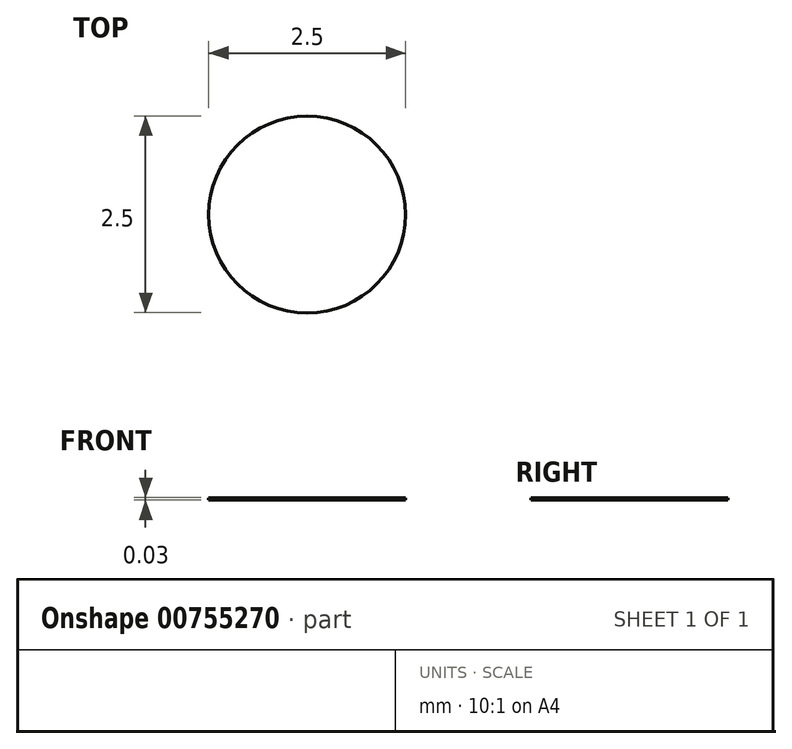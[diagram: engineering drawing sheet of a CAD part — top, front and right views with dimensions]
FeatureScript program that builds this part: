
annotation { "Feature Type Name" : "Feature", "Feature Type Description" : "" }
export const myFeature = defineFeature(function(context is Context, id is Id, definition is map)
    precondition{}
    {
        {
            var Q0;
            Q0=qCreatedBy(makeId("Top.planeOp"),FACE);
            var sketch = newSketch(context, id + "F0", { "sketchPlane" : qUnion([Q0])});
            skCircle(sketch, "E0", {"center": v(-41.46, 15.7) * mm, "radius": 1.25 * mm});
            skSolve(sketch);
        }
        {
            var Q0;
            Q0=makeQuery(id+"F0.imprint","IMPRINT",FACE,{"disambiguationData":[TD([[makeQuery(id+"F0.imprint","IMPRINT",EDGE,{"derivedFrom":sQuery(id+"F0.wireOp",EDGE,"E0")}),1.0]])]});
            extrude(context, id + "F1", {"entities" : qUnion([Q0]), "depth" : 3 / 101.6 * mm, "offsetDistance" : 25 * mm});
        }
    });
